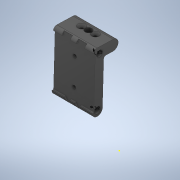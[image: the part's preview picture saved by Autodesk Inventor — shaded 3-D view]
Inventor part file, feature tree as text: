
AUTODESK INVENTOR PART (.ipt)
format: ipt  version: 2020 (Build 240168000, 168)  size: 340,480 bytes
history: native  units: in
note: dims shown in document units (in); Inventor stores cm internally (conversion verified against a paired STEP export)
features: extrude x6, sketch x6, projected_geometry x2
ambient origin geometry x8: Origin, YZ Plane, XZ Plane, XY Plane, X Axis, Y Axis, Z Axis, Center Point
bodies: Solid2 (feature_tree), Solid1 (feature_tree)
feature tree (14):
  extrude  "Extrusion1"  Depth=0.126in
  extrude  "add 5mm left"  Depth=0.1969in TaperAngle=0.0deg
  extrude  "add 5mm right"  Depth=0.1181in
  extrude  "fin mount holes"  Depth=0.3937in TaperAngle=0.0deg
  extrude  "add standoff holes"  Depth=0.2087in
  extrude  "add nuts for mounting"  Depth=0.2205in
  sketch  "Sketch1"  dims[d0=0.126in d1=0.126in]
  sketch  "Sketch2"  dims[d2=0.3937in d3=0.0in d4=0.1969in d5=0.0in]
  projected_geometry  "Projected Loop1"
  sketch  "Sketch3"  dims[d6=0.1969in d7=0.0in d8=0.1181in]
  projected_geometry  "Projected Loop2"
  sketch  "Sketch4"  dims[d9=0.1181in d10=0.3937in d11=0.0in]
  sketch  "Sketch5"  dims[d12=0.2087in d13=0.2087in]
  sketch  "Sketch6"  dims[d14=0.3937in d15=0.0in d16=0.2205in d17=0.2205in d18=0.0984in d19=0.0in]
